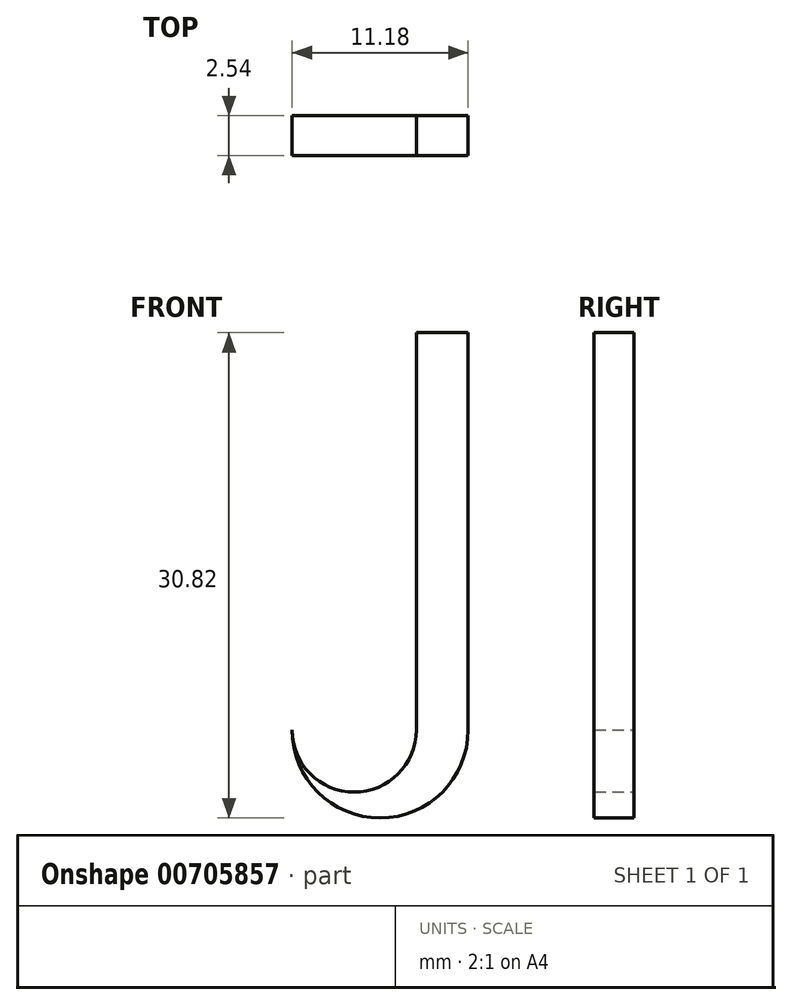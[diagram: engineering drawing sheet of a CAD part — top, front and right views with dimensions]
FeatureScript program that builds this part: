
annotation { "Feature Type Name" : "Feature", "Feature Type Description" : "" }
export const myFeature = defineFeature(function(context is Context, id is Id, definition is map)
    precondition{}
    {
        {
            var Q0;
            Q0=qCreatedBy(makeId("Front.planeOp"),FACE);
            var sketch = newSketch(context, id + "F0", { "sketchPlane" : qUnion([Q0])});
            skLineSegment(sketch, "E0", {"start": v(-16.34, 0) * mm, "end": v(-16.34, -25.23) * mm});
            skLineSegment(sketch, "E1", {"start": v(-19.63, 0) * mm, "end": v(-19.63, -25.23) * mm});
            skArc(sketch, "E2", {"start": v(-27.52, -25.23) * mm, "mid": v(-21.93, -30.82) * mm, "end": v(-16.34, -25.23) * mm});
            skArc(sketch, "E3", {"start": v(-27.52, -25.23) * mm, "mid": v(-23.58, -29.18) * mm, "end": v(-19.63, -25.23) * mm});
            skLineSegment(sketch, "E4", {"start": v(-19.63, 0) * mm, "end": v(-16.34, 0) * mm});
            skSolve(sketch);
        }
        {
            var Q0;
            Q0 = qSketchRegion(id + "F0", true);
            extrude(context, id + "F1", {"entities" : qUnion([Q0]), "depth" : 2.54 * mm, "offsetDistance" : 25.4 * mm});
        }
    });
